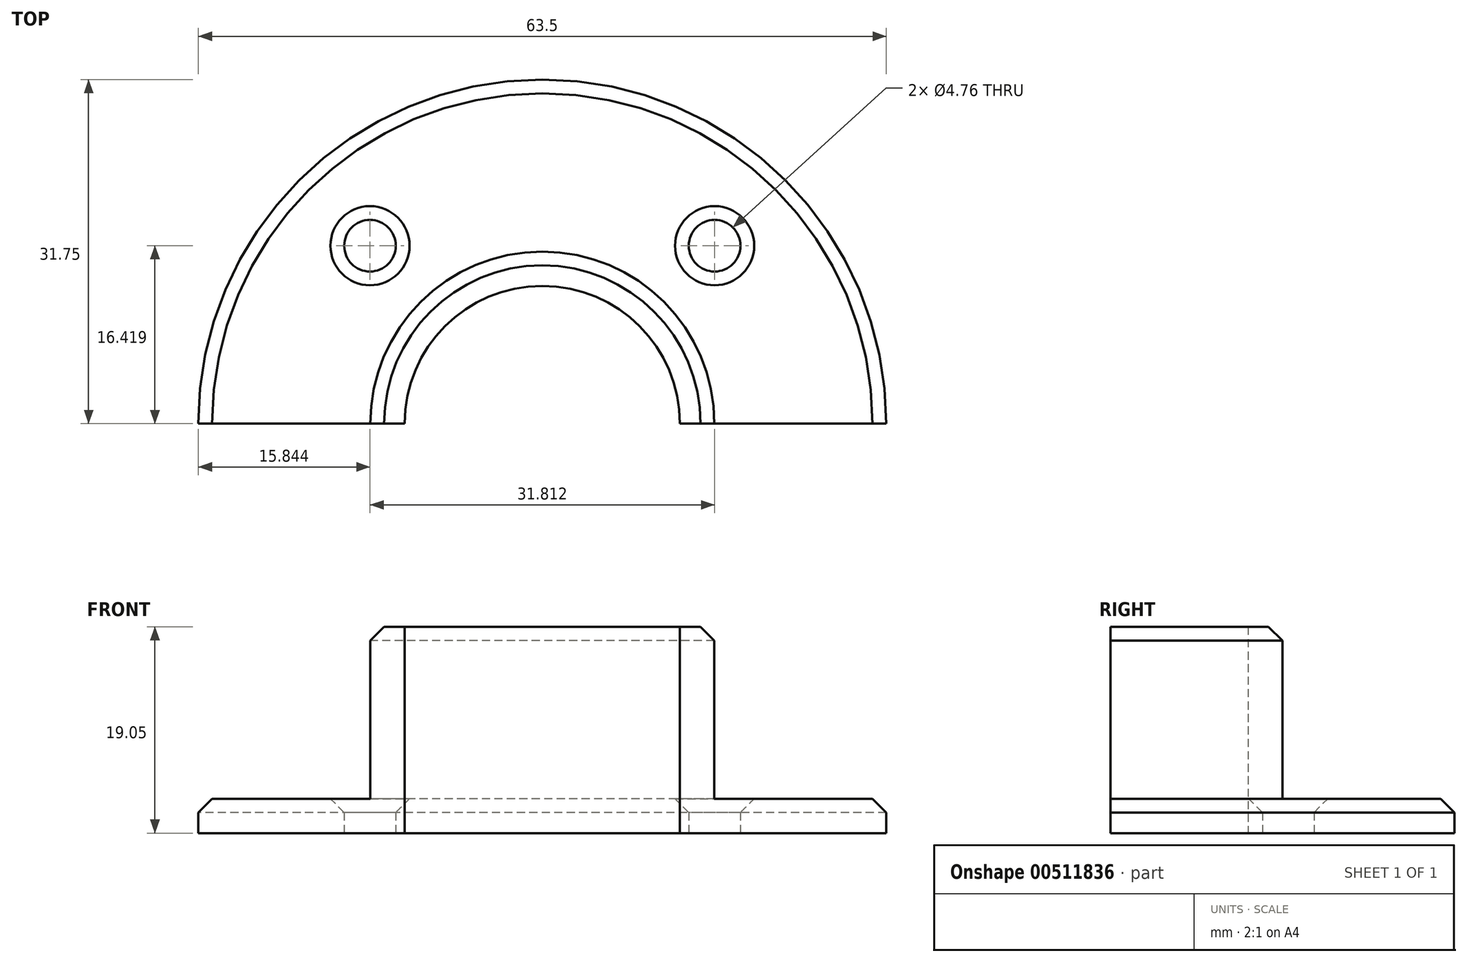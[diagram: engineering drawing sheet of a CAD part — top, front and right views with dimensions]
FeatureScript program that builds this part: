
annotation { "Feature Type Name" : "Feature", "Feature Type Description" : "" }
export const myFeature = defineFeature(function(context is Context, id is Id, definition is map)
    precondition{}
    {
        {
            var Q0;
            Q0=qCreatedBy(makeId("Top.planeOp"),FACE);
            var sketch = newSketch(context, id + "F0", { "sketchPlane" : qUnion([Q0])});
            skLineSegment(sketch, "E0", {"start": v(84.1, 0) * mm, "end": v(-83.06, 0) * mm});
            skCircle(sketch, "E1", {"center": v(0, 0) * mm, "radius": 12.7 * mm});
            skCircle(sketch, "E2", {"center": v(0, 0) * mm, "radius": 31.75 * mm});
            skLineSegment(sketch, "E3", {"start": v(0, 66.5) * mm, "end": v(0, -63.3) * mm, "construction": true});
            skCircle(sketch, "E4", {"center": v(-15.9, 16.42) * mm, "radius": 2.38 * mm});
            skCircle(sketch, "E5", {"center": v(0, 0) * mm, "radius": 22.86 * mm, "construction": true});
            skCircle(sketch, "E6.MirrorC", {"center": v(15.9, 16.42) * mm, "radius": 2.38 * mm});
            skCircle(sketch, "E7", {"center": v(0, 0) * mm, "radius": 15.88 * mm});
            skSolve(sketch);
        }
        {
            var Q0;
            Q0=makeQuery(id+"F0.imprint","IMPRINT",FACE,{"disambiguationData":[TD([[makeQuery(id+"F0.imprint","IMPRINT",EDGE,{"derivedFrom":sQuery(id+"F0.wireOp",EDGE,"E4")}),-1.0]])]});
            extrude(context, id + "F1", {"entities" : qUnion([Q0]), "depth" : 3.17 * mm, "offsetDistance" : 25.4 * mm});
        }
        {
            var Q0;
            {var subQ0=sQuery(id+"F0.wireOp",EDGE,"E7");var subQ1=sQuery(id+"F0.wireOp",EDGE,"E0");var subQ2=makeQuery(id+"F0.imprint","INTERSECT",VERTEX,{"disambiguationData":[OD(0.0)],"derivedFrom":[subQ1,subQ0]});Q0=makeQuery(id+"F0.imprint","IMPRINT",FACE,{"disambiguationData":[TD([[makeQuery(id+"F0.imprint","IMPRINT",EDGE,{"disambiguationData":[TD([[subQ2,-1.0]])],"derivedFrom":subQ1}),-1.0]])]});}
            extrude(context, id + "F2", {"entities" : qUnion([Q0]), "operationType" : NewBodyOperationType.ADD, "depth" : 19.05 * mm, "offsetDistance" : 25.4 * mm});
        }
        {
            var Q0;
            Q0=makeQuery(id+"F1.opExtrude","CAP_EDGE",EDGE,{"disambiguationData":[OSD([sQuery(id+"F0.wireOp",EDGE,"E4")])],"isStart":false});
            var Q1;
            Q1=makeQuery(id+"F1.opExtrude","CAP_EDGE",EDGE,{"disambiguationData":[OSD([sQuery(id+"F0.wireOp",EDGE,"E6.MirrorC")])],"isStart":false});
            var Q2;
            Q2=makeQuery(id+"F1.opExtrude","CAP_EDGE",EDGE,{"disambiguationData":[OSD([sQuery(id+"F0.wireOp",EDGE,"E2")])],"isStart":false});
            var Q3;
            Q3=makeQuery(id+"F2.opExtrude","CAP_EDGE",EDGE,{"disambiguationData":[OSD([sQuery(id+"F0.wireOp",EDGE,"E7")])],"isStart":false});
            var Q4;
            Q4=makeQuery(id+"F1.opExtrude","CAP_EDGE",EDGE,{"disambiguationData":[OSD([sQuery(id+"F0.wireOp",EDGE,"E7")])],"isStart":false});
            chamfer(context, id + "F3", {"entities" : qUnion([Q0, Q1, Q2, Q3, Q4]), "width" : 1.27 * mm, "tangentPropagation" : true});
        }
    });
